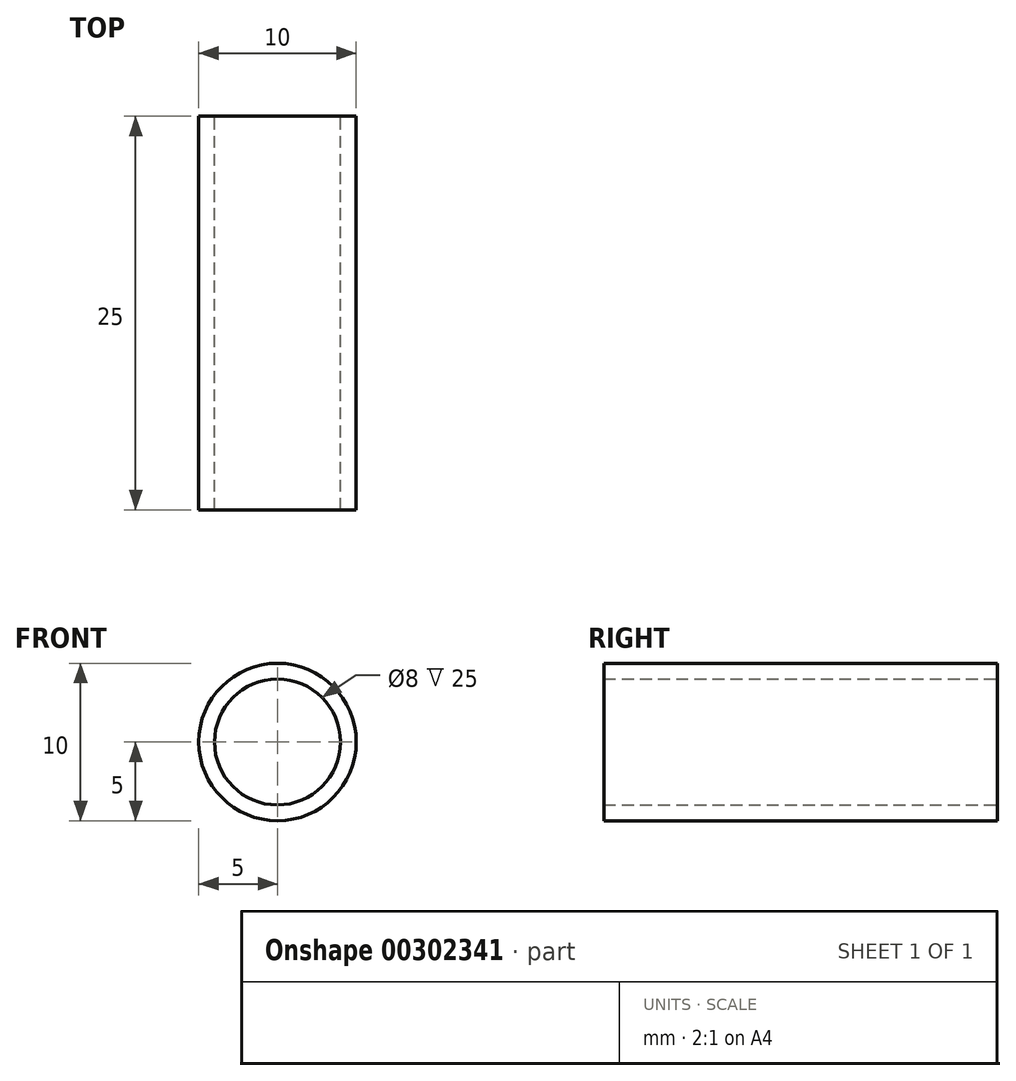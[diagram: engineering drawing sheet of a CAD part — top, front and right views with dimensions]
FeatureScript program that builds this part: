
annotation { "Feature Type Name" : "Feature", "Feature Type Description" : "" }
export const myFeature = defineFeature(function(context is Context, id is Id, definition is map)
    precondition{}
    {
        {
            var Q0;
            Q0=qCreatedBy(makeId("Front.planeOp"),FACE);
            var sketch = newSketch(context, id + "F0", { "sketchPlane" : qUnion([Q0])});
            skCircle(sketch, "E0", {"center": v(0, 0) * mm, "radius": 5 * mm});
            skCircle(sketch, "E1", {"center": v(0, 0) * mm, "radius": 4 * mm});
            skLineSegment(sketch, "E2", {"start": v(0, 0) * mm, "end": v(0, 12) * mm, "construction": true});
            skLineSegment(sketch, "E3", {"start": v(0, 0) * mm, "end": v(-14.01, 0) * mm, "construction": true});
            skSolve(sketch);
        }
        {
            var Q0;
            Q0 = qSketchRegion(id + "F0", true);
            extrude(context, id + "F1", {"entities" : qUnion([Q0]), "depth" : 25 * mm});
        }
    });
